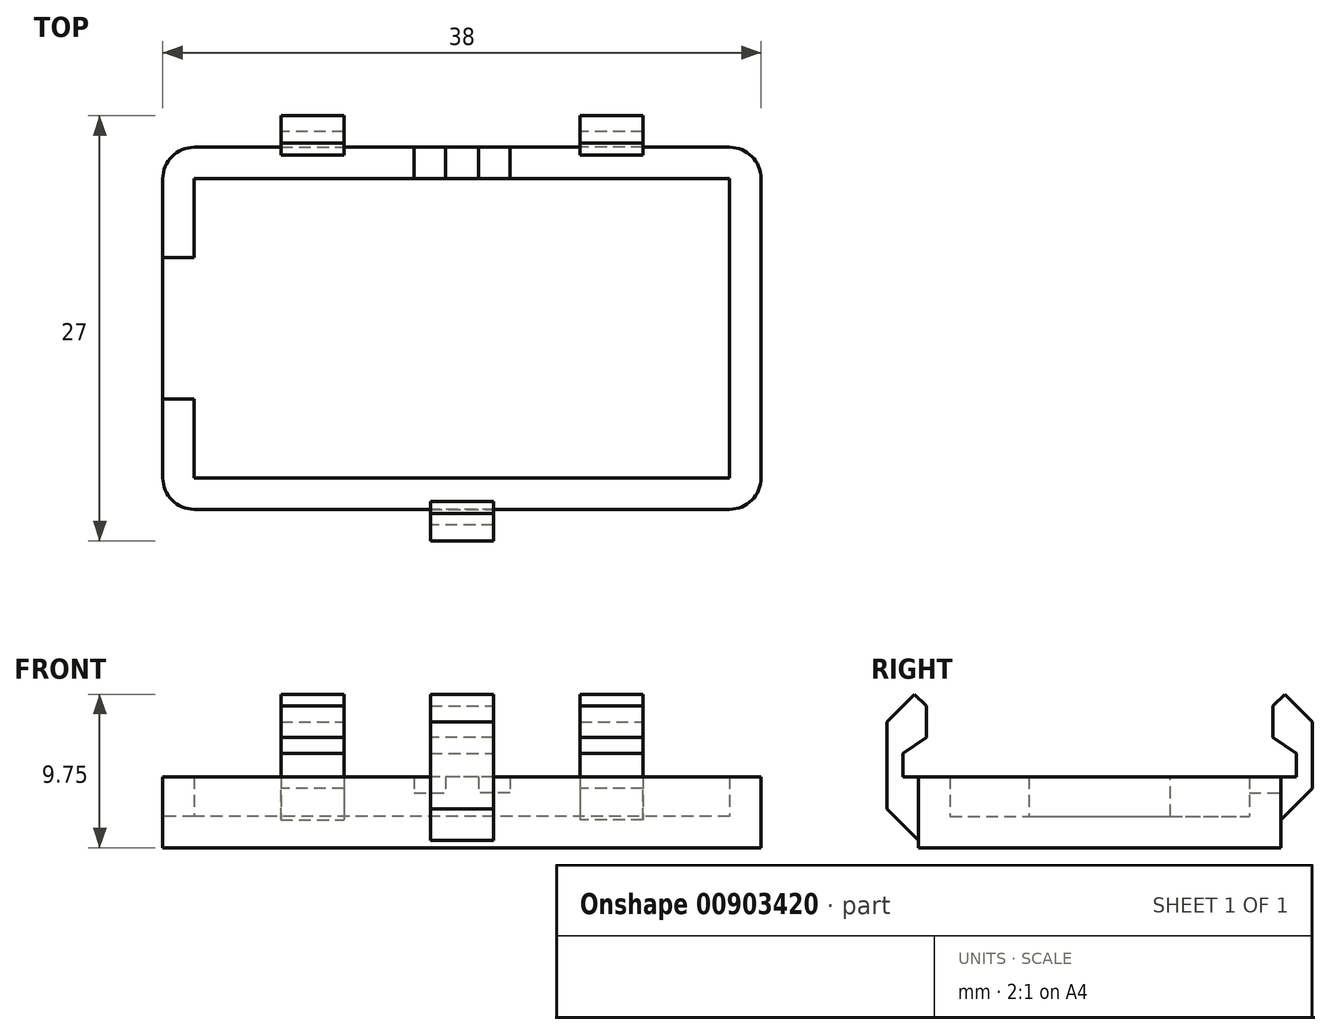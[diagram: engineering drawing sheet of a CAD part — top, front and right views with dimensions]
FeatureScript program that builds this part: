
annotation { "Feature Type Name" : "Feature", "Feature Type Description" : "" }
export const myFeature = defineFeature(function(context is Context, id is Id, definition is map)
    precondition{}
    {
        {
            var Q0;
            Q0=qCreatedBy(makeId("Top.planeOp"),FACE);
            var sketch = newSketch(context, id + "F0", { "sketchPlane" : qUnion([Q0])});
            skLineSegment(sketch, "E0.bottom", {"start": v(19, -11.5) * mm, "end": v(-19, -11.5) * mm});
            skLineSegment(sketch, "E0.top", {"start": v(19, 11.5) * mm, "end": v(-19, 11.5) * mm});
            skLineSegment(sketch, "E0.left", {"start": v(19, -11.5) * mm, "end": v(19, 11.5) * mm});
            skLineSegment(sketch, "E0.right", {"start": v(-19, -11.5) * mm, "end": v(-19, 11.5) * mm});
            skPoint(sketch, "E0.middle", {"position": v(0, 0) * mm});
            skSolve(sketch);
        }
        {
            var Q0;
            Q0=makeQuery(id+"F0.imprint","IMPRINT",FACE,{"disambiguationData":[TD([[makeQuery(id+"F0.imprint","IMPRINT",EDGE,{"derivedFrom":sQuery(id+"F0.wireOp",EDGE,"E0.bottom")}),-1.0]])]});
            extrude(context, id + "F1", {"entities" : qUnion([Q0]), "depth" : 4.5 * mm, "offsetDistance" : 25 * mm});
        }
        {
            var Q0;
            Q0=makeQuery(id+"F1.opExtrude","CAP_FACE",FACE,{"disambiguationData":[OSD([sQuery(id+"F0.wireOp",EDGE,"E0.bottom"),sQuery(id+"F0.wireOp",EDGE,"E0.top"),sQuery(id+"F0.wireOp",EDGE,"E0.left"),sQuery(id+"F0.wireOp",EDGE,"E0.right")])],"isStart":false});
            shell(context, id + "F2", {"entities" : qUnion([Q0]), "thickness" : 2 * mm});
        }
        {
            var Q0;
            Q0=makeQuery(id+"F1.opExtrude","SWEPT_FACE",FACE,{"disambiguationData":[OSD([sQuery(id+"F0.wireOp",EDGE,"E0.right")])]});
            var sketch = newSketch(context, id + "F3", { "sketchPlane" : qUnion([Q0])});
            skLineSegment(sketch, "E1", {"start": v(11.5, 4.5) * mm, "end": v(-11.5, 0) * mm, "construction": true});
            skLineSegment(sketch, "E2", {"start": v(-11.5, 4.5) * mm, "end": v(11.5, 0) * mm, "construction": true});
            skPoint(sketch, "E3", {"position": v(0, 2.25) * mm});
            skLineSegment(sketch, "E4.bottom", {"start": v(4.5, 2) * mm, "end": v(-4.5, 2) * mm});
            skLineSegment(sketch, "E4.top", {"start": v(4.5, 7) * mm, "end": v(-4.5, 7) * mm});
            skLineSegment(sketch, "E4.left", {"start": v(4.5, 2) * mm, "end": v(4.5, 7) * mm});
            skLineSegment(sketch, "E4.right", {"start": v(-4.5, 2) * mm, "end": v(-4.5, 7) * mm});
            skPoint(sketch, "E4.middle", {"position": v(0, 4.5) * mm});
            skSolve(sketch);
        }
        {
            var Q0;
            {var subQ0=sQuery(id+"F3.wireOp",EDGE,"E4.bottom");Q0=makeQuery(id+"F3.imprint","IMPRINT",FACE,{"disambiguationData":[TD([[makeQuery(id+"F3.imprint","IMPRINT",EDGE,{"derivedFrom":subQ0}),-1.0]])]});}
            extrude(context, id + "F4", {"entities" : qUnion([Q0]), "operationType" : NewBodyOperationType.REMOVE, "endBound" : BoundingType.UP_TO_NEXT, "oppositeDirection" : true, "depth" : 25 * mm, "offsetDistance" : 25 * mm});
        }
        {
            var Q0;
            Q0=makeQuery(id+"F1.opExtrude","SWEPT_FACE",FACE,{"disambiguationData":[OSD([sQuery(id+"F0.wireOp",EDGE,"E0.top")])]});
            var sketch = newSketch(context, id + "F5", { "sketchPlane" : qUnion([Q0])});
            skLineSegment(sketch, "E5", {"start": v(0, 0) * mm, "end": v(0, 4.5) * mm, "construction": true});
            skLineSegment(sketch, "E6.bottom", {"start": v(-3.04, 4.5) * mm, "end": v(-1.04, 4.5) * mm});
            skLineSegment(sketch, "E6.top", {"start": v(-3.04, 3.5) * mm, "end": v(-1.04, 3.5) * mm});
            skLineSegment(sketch, "E6.left", {"start": v(-3.04, 4.5) * mm, "end": v(-3.04, 3.5) * mm});
            skLineSegment(sketch, "E6.right", {"start": v(-1.04, 4.5) * mm, "end": v(-1.04, 3.5) * mm});
            skLineSegment(sketch, "E7.MirrorCS", {"start": v(1.04, 4.5) * mm, "end": v(1.04, 3.5) * mm});
            skLineSegment(sketch, "E8.MirrorCS", {"start": v(3.04, 3.5) * mm, "end": v(1.04, 3.5) * mm});
            skLineSegment(sketch, "E9.MirrorCS", {"start": v(3.04, 4.5) * mm, "end": v(3.04, 3.5) * mm});
            skSolve(sketch);
        }
        {
            var Q0;
            Q0 = qSketchRegion(id + "F5", true);
            var Q1;
            {var subQ0=sQuery(id+"F5.wireOp",EDGE,"E7.MirrorCS");Q1=makeQuery(id+"F5.imprint","IMPRINT",FACE,{"disambiguationData":[TD([[makeQuery(id+"F5.imprint","IMPRINT",EDGE,{"derivedFrom":subQ0}),1.0]])]});}
            extrude(context, id + "F6", {"entities" : qUnion([Q0, Q1]), "operationType" : NewBodyOperationType.REMOVE, "endBound" : BoundingType.UP_TO_NEXT, "oppositeDirection" : true, "depth" : 25 * mm, "offsetDistance" : 25 * mm});
        }
        {
            var Q0;
            Q0=makeQuery(id+"F1.opExtrude","SWEPT_FACE",FACE,{"disambiguationData":[OSD([sQuery(id+"F0.wireOp",EDGE,"E0.top")])]});
            var sketch = newSketch(context, id + "F7", { "sketchPlane" : qUnion([Q0])});
            skLineSegment(sketch, "E10", {"start": v(-19, 0) * mm, "end": v(19, 4.5) * mm, "construction": true});
            skLineSegment(sketch, "E11", {"start": v(19, 4.5) * mm, "end": v(19, 0) * mm, "construction": true});
            skLineSegment(sketch, "E12", {"start": v(19, 0) * mm, "end": v(-19, 4.5) * mm, "construction": true});
            skLineSegment(sketch, "E13", {"start": v(-19, 4.5) * mm, "end": v(0, 0) * mm, "construction": true});
            skLineSegment(sketch, "E14", {"start": v(0, 0) * mm, "end": v(0, 4.5) * mm, "construction": true});
            skLineSegment(sketch, "E15", {"start": v(0, 4.5) * mm, "end": v(-19, 0) * mm, "construction": true});
            skLineSegment(sketch, "E16", {"start": v(0, 4.5) * mm, "end": v(19, 0) * mm, "construction": true});
            skLineSegment(sketch, "E17", {"start": v(19, 4.5) * mm, "end": v(0, 0) * mm, "construction": true});
            skLineSegment(sketch, "E18.bottom", {"start": v(-7.5, 10) * mm, "end": v(-11.5, 10) * mm});
            skLineSegment(sketch, "E18.left", {"start": v(-7.5, 10) * mm, "end": v(-7.5, 1.78) * mm});
            skLineSegment(sketch, "E18.right", {"start": v(-11.5, 10) * mm, "end": v(-11.5, 1.78) * mm});
            skPoint(sketch, "E18.middle", {"position": v(-9.5, 2.25) * mm});
            skLineSegment(sketch, "E19", {"start": v(-11.5, 1.78) * mm, "end": v(-7.5, 1.78) * mm});
            skPoint(sketch, "E20", {"position": v(-11.5, 4.5) * mm});
            skPoint(sketch, "E21", {"position": v(-7.5, 4.5) * mm});
            skLineSegment(sketch, "E22", {"start": v(-11.5, 6) * mm, "end": v(-7.5, 6) * mm});
            skLineSegment(sketch, "E23.MirrorCS", {"start": v(7.5, 10) * mm, "end": v(7.5, 1.78) * mm});
            skLineSegment(sketch, "E24.MirrorCS", {"start": v(7.5, 10) * mm, "end": v(11.5, 10) * mm});
            skLineSegment(sketch, "E25.MirrorCS", {"start": v(11.5, 10) * mm, "end": v(11.5, 1.78) * mm});
            skLineSegment(sketch, "E26.MirrorCS", {"start": v(11.5, 6) * mm, "end": v(7.5, 6) * mm});
            skLineSegment(sketch, "E27.MirrorCS", {"start": v(11.5, 1.78) * mm, "end": v(7.5, 1.78) * mm});
            skPoint(sketch, "E18.top.end.orphan", {"position": v(-11.5, -5.5) * mm});
            skPoint(sketch, "E18.top.start.orphan", {"position": v(-7.5, -5.5) * mm});
            skSolve(sketch);
        }
        {
            var Q0;
            Q0 = qSketchRegion(id + "F7", true);
            extrude(context, id + "F8", {"entities" : qUnion([Q0]), "operationType" : NewBodyOperationType.ADD, "depth" : 2 * mm, "offsetDistance" : 25 * mm});
        }
        {
            var Q0;
            {var subQ0=sQuery(id+"F7.wireOp",EDGE,"E18.bottom");Q0=makeQuery(id+"F7.imprint","IMPRINT",FACE,{"disambiguationData":[TD([[makeQuery(id+"F7.imprint","IMPRINT",EDGE,{"derivedFrom":subQ0}),1.0]])]});}
            var Q1;
            {var subQ0=sQuery(id+"F7.wireOp",EDGE,"E24.MirrorCS");Q1=makeQuery(id+"F7.imprint","IMPRINT",FACE,{"disambiguationData":[TD([[makeQuery(id+"F7.imprint","IMPRINT",EDGE,{"derivedFrom":subQ0}),-1.0]])]});}
            extrude(context, id + "F9", {"entities" : qUnion([Q0, Q1]), "operationType" : NewBodyOperationType.ADD, "oppositeDirection" : true, "depth" : .5 * mm, "offsetDistance" : 25 * mm});
        }
        {
            var Q0;
            Q0=makeQuery(id+"F1.opExtrude","SWEPT_FACE",FACE,{"disambiguationData":[OSD([sQuery(id+"F0.wireOp",EDGE,"E0.bottom")])]});
            var sketch = newSketch(context, id + "F10", { "sketchPlane" : qUnion([Q0])});
            skLineSegment(sketch, "E28", {"start": v(-19, 4.5) * mm, "end": v(19, 0) * mm, "construction": true});
            skLineSegment(sketch, "E29", {"start": v(19, 0) * mm, "end": v(19, 4.5) * mm, "construction": true});
            skLineSegment(sketch, "E30", {"start": v(19, 4.5) * mm, "end": v(-19, 0) * mm, "construction": true});
            skLineSegment(sketch, "E31.bottom", {"start": v(2, 10) * mm, "end": v(-2, 10) * mm});
            skLineSegment(sketch, "E31.left", {"start": v(2, 10) * mm, "end": v(2, 0.46) * mm});
            skLineSegment(sketch, "E31.right", {"start": v(-2, 10) * mm, "end": v(-2, 0.46) * mm});
            skPoint(sketch, "E31.middle", {"position": v(0, 2.25) * mm});
            skLineSegment(sketch, "E32", {"start": v(-2, 6) * mm, "end": v(2, 6) * mm});
            skLineSegment(sketch, "E33", {"start": v(-2, 0.46) * mm, "end": v(2, 0.46) * mm});
            skPoint(sketch, "E31.top.end.orphan", {"position": v(-2, -5.5) * mm});
            skPoint(sketch, "E31.top.start.orphan", {"position": v(2, -5.5) * mm});
            skSolve(sketch);
        }
        {
            var Q0;
            Q0 = qSketchRegion(id + "F10", true);
            extrude(context, id + "F11", {"entities" : qUnion([Q0]), "operationType" : NewBodyOperationType.ADD, "depth" : 2 * mm, "offsetDistance" : 25 * mm});
        }
        {
            var Q0;
            {var subQ0=sQuery(id+"F10.wireOp",EDGE,"E31.bottom");Q0=makeQuery(id+"F10.imprint","IMPRINT",FACE,{"disambiguationData":[TD([[makeQuery(id+"F10.imprint","IMPRINT",EDGE,{"derivedFrom":subQ0}),1.0]])]});}
            extrude(context, id + "F12", {"entities" : qUnion([Q0]), "operationType" : NewBodyOperationType.ADD, "oppositeDirection" : true, "depth" : .5 * mm, "offsetDistance" : 25 * mm});
        }
        {
            var Q0;
            Q0=makeQuery(id+"F12.opExtrude","CAP_EDGE",EDGE,{"disambiguationData":[OSD([sQuery(id+"F10.wireOp",EDGE,"E31.bottom")])],"isStart":false});
            var Q1;
            Q1=makeQuery(id+"F9.opExtrude","CAP_EDGE",EDGE,{"disambiguationData":[OSD([sQuery(id+"F7.wireOp",EDGE,"E24.MirrorCS")])],"isStart":false});
            var Q2;
            Q2=makeQuery(id+"F9.opExtrude","CAP_EDGE",EDGE,{"disambiguationData":[OSD([sQuery(id+"F7.wireOp",EDGE,"E18.bottom")])],"isStart":false});
            chamfer(context, id + "F13", {"entities" : qUnion([Q0, Q1, Q2]), "chamferType" : ChamferType.OFFSET_ANGLE, "width" : 1 * mm, "oppositeDirection" : false, "angle" : 45 * degree, "tangentPropagation" : true});
        }
        {
            var Q0;
            Q0=makeQuery(id+"F8.opExtrude","CAP_EDGE",EDGE,{"disambiguationData":[OSD([sQuery(id+"F7.wireOp",EDGE,"E27.MirrorCS")])],"isStart":false});
            var Q1;
            Q1=makeQuery(id+"F8.opExtrude","CAP_EDGE",EDGE,{"disambiguationData":[OSD([sQuery(id+"F7.wireOp",EDGE,"E19")])],"isStart":false});
            var Q2;
            Q2=makeQuery(id+"F11.opExtrude","CAP_EDGE",EDGE,{"disambiguationData":[OSD([sQuery(id+"F10.wireOp",EDGE,"E33")])],"isStart":false});
            var Q3;
            Q3=makeQuery(id+"F8.opExtrude","CAP_EDGE",EDGE,{"disambiguationData":[OSD([sQuery(id+"F7.wireOp",EDGE,"E18.bottom")])],"isStart":false});
            var Q4;
            Q4=makeQuery(id+"F8.opExtrude","CAP_EDGE",EDGE,{"disambiguationData":[OSD([sQuery(id+"F7.wireOp",EDGE,"E24.MirrorCS")])],"isStart":false});
            var Q5;
            Q5=makeQuery(id+"F11.opExtrude","CAP_EDGE",EDGE,{"disambiguationData":[OSD([sQuery(id+"F10.wireOp",EDGE,"E31.bottom")])],"isStart":false});
            chamfer(context, id + "F14", {"entities" : qUnion([Q0, Q1, Q2, Q3, Q4, Q5]), "chamferType" : ChamferType.OFFSET_ANGLE, "width" : 2 * mm, "oppositeDirection" : false, "angle" : 45 * degree, "tangentPropagation" : true});
        }
        {
            var Q0;
            Q0=makeQuery(id+"F1.opExtrude","SWEPT_EDGE",EDGE,{"disambiguationData":[OSD([sQuery(id+"F0.wireOp",EDGE,"E0.bottom"),sQuery(id+"F0.wireOp",EDGE,"E0.left")])]});
            var Q1;
            Q1=makeQuery(id+"F1.opExtrude","SWEPT_EDGE",EDGE,{"disambiguationData":[OSD([sQuery(id+"F0.wireOp",EDGE,"E0.top"),sQuery(id+"F0.wireOp",EDGE,"E0.left")])]});
            var Q2;
            Q2=makeQuery(id+"F1.opExtrude","SWEPT_EDGE",EDGE,{"disambiguationData":[OSD([sQuery(id+"F0.wireOp",EDGE,"E0.top"),sQuery(id+"F0.wireOp",EDGE,"E0.right")])]});
            var Q3;
            Q3=makeQuery(id+"F1.opExtrude","SWEPT_EDGE",EDGE,{"disambiguationData":[OSD([sQuery(id+"F0.wireOp",EDGE,"E0.bottom"),sQuery(id+"F0.wireOp",EDGE,"E0.right")])]});
            fillet(context, id + "F15", {"entities" : qUnion([Q0, Q1, Q2, Q3]), "radius" : 2 * mm, "tangentPropagation" : true, "allowEdgeOverflow" : false});
        }
        {
            var Q0;
            {var subQ0=sQuery(id+"F10.wireOp",EDGE,"E32");Q0=makeQuery(id+"F10.imprint","IMPRINT",FACE,{"disambiguationData":[TD([[makeQuery(id+"F10.imprint","IMPRINT",EDGE,{"derivedFrom":subQ0}),-1.0]])]});}
            extrude(context, id + "F16", {"entities" : qUnion([Q0]), "operationType" : NewBodyOperationType.REMOVE, "depth" : 1 * mm, "offsetDistance" : 25 * mm});
        }
        {
            var Q0;
            {var subQ0=sQuery(id+"F7.wireOp",EDGE,"E26.MirrorCS");Q0=makeQuery(id+"F7.imprint","IMPRINT",FACE,{"disambiguationData":[TD([[makeQuery(id+"F7.imprint","IMPRINT",EDGE,{"derivedFrom":subQ0}),1.0]])]});}
            var Q1;
            {var subQ0=sQuery(id+"F7.wireOp",EDGE,"E22");Q1=makeQuery(id+"F7.imprint","IMPRINT",FACE,{"disambiguationData":[TD([[makeQuery(id+"F7.imprint","IMPRINT",EDGE,{"derivedFrom":subQ0}),-1.0]])]});}
            extrude(context, id + "F17", {"entities" : qUnion([Q0, Q1]), "operationType" : NewBodyOperationType.REMOVE, "depth" : 1 * mm, "offsetDistance" : 25 * mm});
        }
        {
            var Q0;
            Q0=makeQuery(id+"F12.opExtrude","CAP_EDGE",EDGE,{"disambiguationData":[OSD([sQuery(id+"F10.wireOp",EDGE,"E32")])],"isStart":false});
            chamfer(context, id + "F18", {"entities" : qUnion([Q0]), "chamferType" : ChamferType.TWO_OFFSETS, "width1" : 1.5 * mm, "oppositeDirection" : false, "width2" : 1 * mm, "tangentPropagation" : true});
        }
        {
            var Q0;
            Q0=makeQuery(id+"F9.opExtrude","CAP_EDGE",EDGE,{"disambiguationData":[OSD([sQuery(id+"F7.wireOp",EDGE,"E26.MirrorCS")])],"isStart":false});
            chamfer(context, id + "F19", {"entities" : qUnion([Q0]), "chamferType" : ChamferType.TWO_OFFSETS, "width1" : 1 * mm, "oppositeDirection" : false, "width2" : 1.5 * mm, "tangentPropagation" : true});
        }
        {
            var Q0;
            Q0=makeQuery(id+"F9.opExtrude","CAP_EDGE",EDGE,{"disambiguationData":[OSD([sQuery(id+"F7.wireOp",EDGE,"E22")])],"isStart":false});
            chamfer(context, id + "F20", {"entities" : qUnion([Q0]), "chamferType" : ChamferType.TWO_OFFSETS, "width1" : 1.5 * mm, "oppositeDirection" : false, "width2" : 1 * mm, "tangentPropagation" : true});
        }
    });
